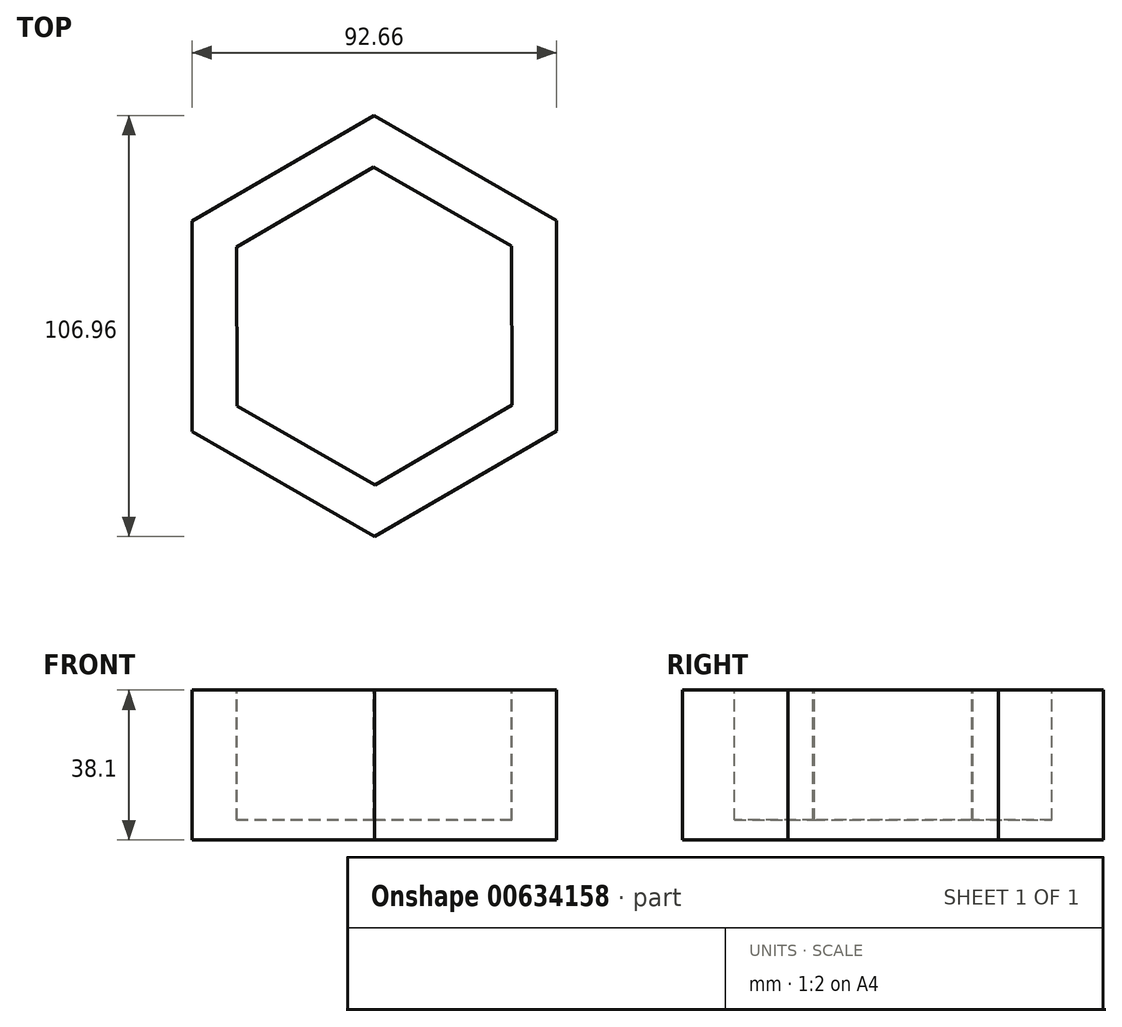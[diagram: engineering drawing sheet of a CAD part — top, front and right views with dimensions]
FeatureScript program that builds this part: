
annotation { "Feature Type Name" : "Feature", "Feature Type Description" : "" }
export const myFeature = defineFeature(function(context is Context, id is Id, definition is map)
    precondition{}
    {
        {
            var Q0;
            Q0=qCreatedBy(makeId("Top.planeOp"),FACE);
            var sketch = newSketch(context, id + "F0", { "sketchPlane" : qUnion([Q0])});
            skCircle(sketch, "E0.cCircle", {"center": v(0, 0) * mm, "radius": 46.32 * mm, "construction": true});
            skLineSegment(sketch, "E0.0", {"start": v(-46.33, 26.72) * mm, "end": v(-0.03, 53.48) * mm});
            skLineSegment(sketch, "E0.1", {"start": v(-0.03, 53.48) * mm, "end": v(46.3, 26.77) * mm});
            skLineSegment(sketch, "E0.2", {"start": v(46.3, 26.77) * mm, "end": v(46.33, -26.72) * mm});
            skLineSegment(sketch, "E0.3", {"start": v(46.33, -26.72) * mm, "end": v(0.03, -53.48) * mm});
            skLineSegment(sketch, "E0.4", {"start": v(0.03, -53.48) * mm, "end": v(-46.3, -26.77) * mm});
            skLineSegment(sketch, "E0.5", {"start": v(-46.3, -26.77) * mm, "end": v(-46.33, 26.72) * mm});
            skPoint(sketch, "E0.0.midPoint", {"position": v(-23.18, 40.1) * mm});
            skSolve(sketch);
        }
        {
            var Q0;
            Q0 = qSketchRegion(id + "F0", true);
            extrude(context, id + "F1", {"entities" : qUnion([Q0]), "depth" : 38.1 * mm, "offsetDistance" : 25.4 * mm});
        }
        {
            var Q0;
            Q0=makeQuery(id+"F1.opExtrude","CAP_FACE",FACE,{"disambiguationData":[OSD([sQuery(id+"F0.wireOp",EDGE,"E0.0"),sQuery(id+"F0.wireOp",EDGE,"E0.1"),sQuery(id+"F0.wireOp",EDGE,"E0.2"),sQuery(id+"F0.wireOp",EDGE,"E0.3"),sQuery(id+"F0.wireOp",EDGE,"E0.4"),sQuery(id+"F0.wireOp",EDGE,"E0.5")])],"isStart":false});
            var sketch = newSketch(context, id + "F2", { "sketchPlane" : qUnion([Q0])});
            skCircle(sketch, "E1.cCircle", {"center": v(0, 0) * mm, "radius": 34.93 * mm, "construction": true});
            skLineSegment(sketch, "E1.0", {"start": v(-0.16, 40.33) * mm, "end": v(34.85, 20.3) * mm});
            skLineSegment(sketch, "E1.1", {"start": v(34.85, 20.3) * mm, "end": v(35, -20.03) * mm});
            skLineSegment(sketch, "E1.2", {"start": v(35, -20.03) * mm, "end": v(0.16, -40.33) * mm});
            skLineSegment(sketch, "E1.3", {"start": v(0.16, -40.33) * mm, "end": v(-34.85, -20.3) * mm});
            skLineSegment(sketch, "E1.4", {"start": v(-34.85, -20.3) * mm, "end": v(-35, 20.03) * mm});
            skLineSegment(sketch, "E1.5", {"start": v(-35, 20.03) * mm, "end": v(-0.16, 40.33) * mm});
            skPoint(sketch, "E1.0.midPoint", {"position": v(17.35, 30.32) * mm});
            skSolve(sketch);
        }
        {
            var Q0;
            Q0 = qSketchRegion(id + "F2", true);
            extrude(context, id + "F3", {"entities" : qUnion([Q0]), "operationType" : NewBodyOperationType.REMOVE, "oppositeDirection" : true, "depth" : 33.02 * mm, "offsetDistance" : 25.4 * mm});
        }
    });
